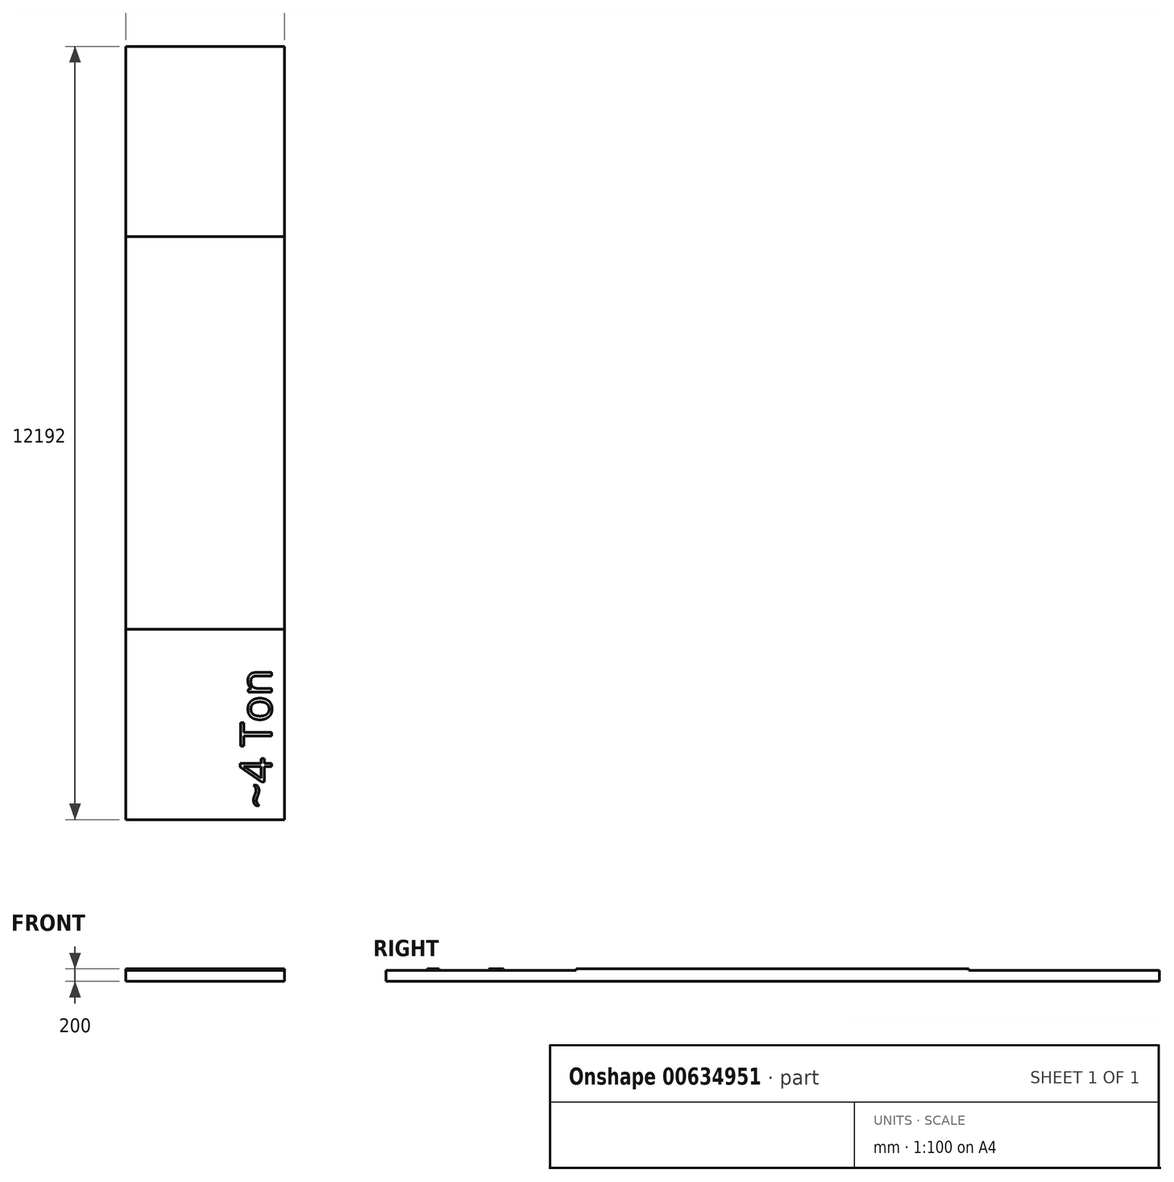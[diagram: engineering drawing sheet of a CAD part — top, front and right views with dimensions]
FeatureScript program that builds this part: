
annotation { "Feature Type Name" : "Feature", "Feature Type Description" : "" }
export const myFeature = defineFeature(function(context is Context, id is Id, definition is map)
    precondition{}
    {
        {
            var Q0;
            Q0=qCreatedBy(makeId("Top.planeOp"),FACE);
            var sketch = newSketch(context, id + "F0", { "sketchPlane" : qUnion([Q0])});
            skLineSegment(sketch, "E0.bottom", {"start": v(-1250, -6096) * mm, "end": v(1250, -6096) * mm});
            skLineSegment(sketch, "E0.top", {"start": v(-1250, 6096) * mm, "end": v(1250, 6096) * mm});
            skLineSegment(sketch, "E0.left", {"start": v(-1250, -6096) * mm, "end": v(-1250, 6096) * mm});
            skLineSegment(sketch, "E0.right", {"start": v(1250, -6096) * mm, "end": v(1250, 6096) * mm});
            skPoint(sketch, "E0.middle", {"position": v(0, 0) * mm});
            skText(sketch, "E1", { "text": "~4 Ton", "fontName": "OpenSans-Regular.ttf"});
            skLineSegment(sketch, "E2.top", {"start": v(-1250, -3096) * mm, "end": v(1250, -3096) * mm});
            skLineSegment(sketch, "E2.left", {"start": v(-1250, -6096) * mm, "end": v(-1250, -3096) * mm});
            skLineSegment(sketch, "E2.right", {"start": v(1250, -6096) * mm, "end": v(1250, -3096) * mm});
            skLineSegment(sketch, "E3.top", {"start": v(-1250, 3096) * mm, "end": v(1250, 3096) * mm});
            skLineSegment(sketch, "E3.left", {"start": v(-1250, 6096) * mm, "end": v(-1250, 3096) * mm});
            skLineSegment(sketch, "E3.right", {"start": v(1250, 6096) * mm, "end": v(1250, 3096) * mm});
            const initialGuessF0  = {"E1": [1.04957, -5.90852, 0, 1, 0.49657]};
            skSetInitialGuess(sketch, initialGuessF0);
            skSolve(sketch);
        }
        {
            var Q0;
            Q0 = qSketchRegion(id + "F0", true);
            var Q1;
            Q1=makeQuery(id+"F0.imprint","IMPRINT",FACE,{"disambiguationData":[TD([[makeQuery(id+"F0.imprint","IMPRINT",EDGE,{"derivedFrom":sQuery(id+"F0.wireOp",EDGE,"E1.sketch_text.stroke-16")}),-1.0]])]});
            var Q2;
            Q2=makeQuery(id+"F0.imprint","IMPRINT",FACE,{"disambiguationData":[TD([[makeQuery(id+"F0.imprint","IMPRINT",EDGE,{"derivedFrom":sQuery(id+"F0.wireOp",EDGE,"E1.sketch_text.stroke-27")}),1.0]])]});
            var Q3;
            Q3=makeQuery(id+"F0.imprint","IMPRINT",FACE,{"disambiguationData":[TD([[makeQuery(id+"F0.imprint","IMPRINT",EDGE,{"derivedFrom":sQuery(id+"F0.wireOp",EDGE,"E1.sketch_text.stroke-0")}),-1.0]])]});
            var Q4;
            Q4=makeQuery(id+"F0.imprint","IMPRINT",FACE,{"disambiguationData":[TD([[makeQuery(id+"F0.imprint","IMPRINT",EDGE,{"derivedFrom":sQuery(id+"F0.wireOp",EDGE,"E1.sketch_text.stroke-33")}),-1.0]])]});
            var Q5;
            Q5=makeQuery(id+"F0.imprint","IMPRINT",FACE,{"disambiguationData":[TD([[makeQuery(id+"F0.imprint","IMPRINT",EDGE,{"derivedFrom":sQuery(id+"F0.wireOp",EDGE,"E1.sketch_text.stroke-41")}),-1.0]])]});
            var Q6;
            Q6=makeQuery(id+"F0.imprint","IMPRINT",FACE,{"disambiguationData":[TD([[makeQuery(id+"F0.imprint","IMPRINT",EDGE,{"derivedFrom":sQuery(id+"F0.wireOp",EDGE,"E1.sketch_text.stroke-50")}),1.0]])]});
            var Q7;
            Q7=makeQuery(id+"F0.imprint","IMPRINT",FACE,{"disambiguationData":[TD([[makeQuery(id+"F0.imprint","IMPRINT",EDGE,{"derivedFrom":sQuery(id+"F0.wireOp",EDGE,"E1.sketch_text.stroke-58")}),-1.0]])]});
            extrude(context, id + "F1", {"entities" : qUnion([Q0, Q1, Q2, Q3, Q4, Q5, Q6, Q7]), "oppositeDirection" : true, "depth" : 200 * mm, "offsetDistance" : 25 * mm});
        }
        {
            var Q0;
            Q0=makeQuery(id+"F0.imprint","IMPRINT",FACE,{"disambiguationData":[TD([[makeQuery(id+"F0.imprint","IMPRINT",EDGE,{"derivedFrom":sQuery(id+"F0.wireOp",EDGE,"E1.sketch_text.stroke-0")}),-1.0]])]});
            var Q1;
            Q1=makeQuery(id+"F0.imprint","IMPRINT",FACE,{"disambiguationData":[TD([[makeQuery(id+"F0.imprint","IMPRINT",EDGE,{"derivedFrom":sQuery(id+"F0.wireOp",EDGE,"E1.sketch_text.stroke-16")}),-1.0]])]});
            var Q2;
            Q2=makeQuery(id+"F0.imprint","IMPRINT",FACE,{"disambiguationData":[TD([[makeQuery(id+"F0.imprint","IMPRINT",EDGE,{"derivedFrom":sQuery(id+"F0.wireOp",EDGE,"E1.sketch_text.stroke-33")}),-1.0]])]});
            var Q3;
            Q3=makeQuery(id+"F0.imprint","IMPRINT",FACE,{"disambiguationData":[TD([[makeQuery(id+"F0.imprint","IMPRINT",EDGE,{"derivedFrom":sQuery(id+"F0.wireOp",EDGE,"E1.sketch_text.stroke-41")}),-1.0]])]});
            var Q4;
            Q4=makeQuery(id+"F0.imprint","IMPRINT",FACE,{"disambiguationData":[TD([[makeQuery(id+"F0.imprint","IMPRINT",EDGE,{"derivedFrom":sQuery(id+"F0.wireOp",EDGE,"E1.sketch_text.stroke-58")}),-1.0]])]});
            extrude(context, id + "F2", {"entities" : qUnion([Q0, Q1, Q2, Q3, Q4]), "operationType" : NewBodyOperationType.REMOVE, "oppositeDirection" : true, "depth" : 35 * mm, "offsetDistance" : 25 * mm});
        }
        {
            var Q0;
            Q0=makeQuery(id+"F0.imprint","IMPRINT",FACE,{"disambiguationData":[TD([[makeQuery(id+"F0.imprint","IMPRINT",EDGE,{"derivedFrom":sQuery(id+"F0.wireOp",EDGE,"E1.sketch_text.stroke-0")}),1.0]])]});
            var Q1;
            Q1=makeQuery(id+"F0.imprint","IMPRINT",FACE,{"disambiguationData":[TD([[makeQuery(id+"F0.imprint","IMPRINT",EDGE,{"derivedFrom":sQuery(id+"F0.wireOp",EDGE,"E0.top")}),-1.0]])]});
            extrude(context, id + "F3", {"entities" : qUnion([Q0, Q1]), "operationType" : NewBodyOperationType.REMOVE, "oppositeDirection" : true, "depth" : 25 * mm, "offsetDistance" : 25 * mm});
        }
    });
